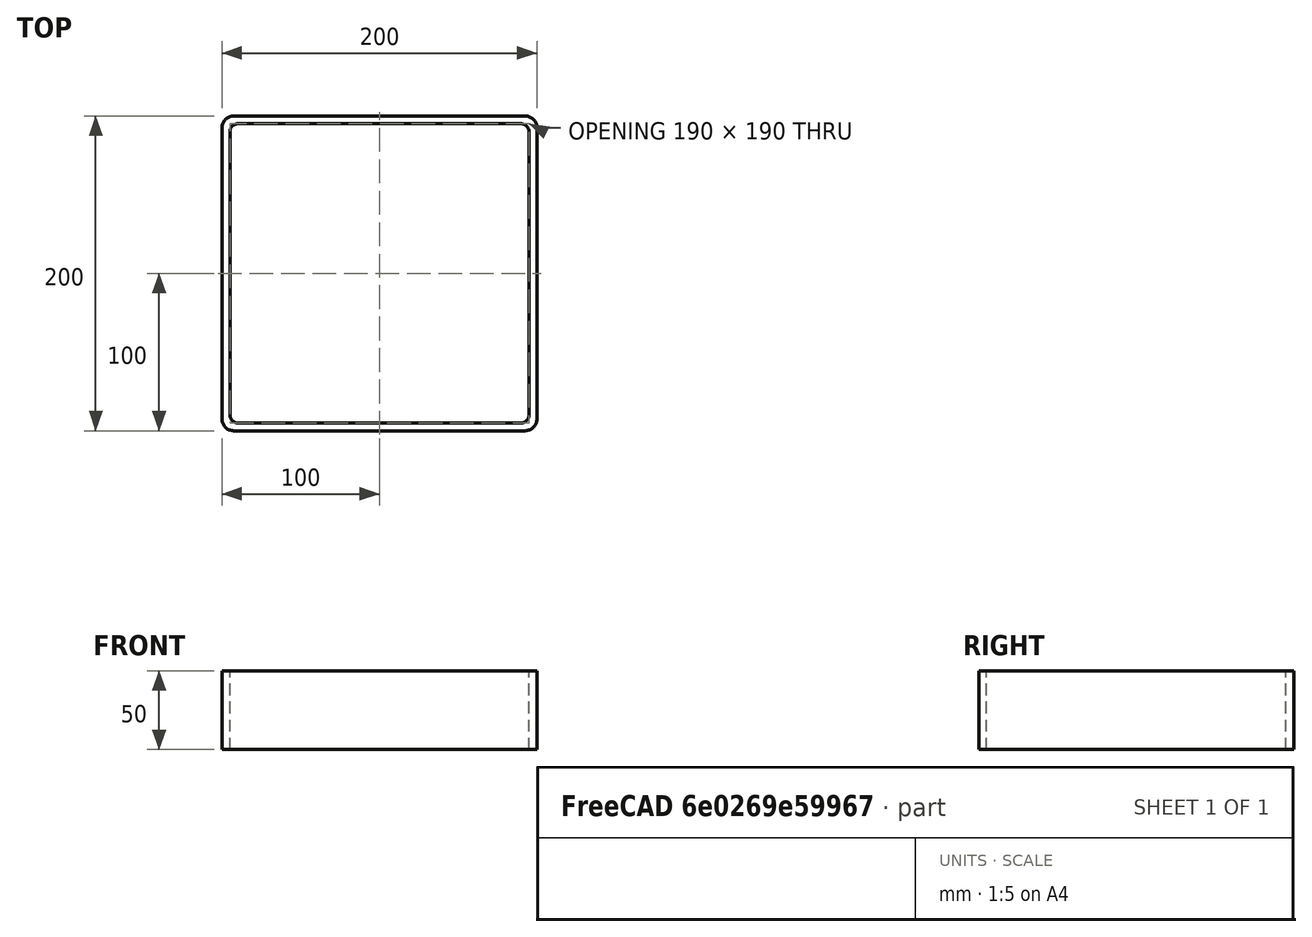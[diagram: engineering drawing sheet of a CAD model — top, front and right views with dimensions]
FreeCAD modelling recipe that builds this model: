
FCSTD DOCUMENT  (FreeCAD 0.15R4671 (Git))
Label: Square hollow section 200x200x5 EN10219 S235JRH
License: All rights reserved
LicenseURL: http://en.wikipedia.org/wiki/All_rights_reserved
objects: Sketcher::SketchObject×1, Part::Extrusion×1
note: 2 computed .brp shape members not serialized (recipe doc carries the construction recipe); baked Part::Feature solids carry a one-line shape summary decoded from their .brp

FEATURE [Sketcher::SketchObject] Sketch
  sketch-geometry (16):
    g0: LineSegment StartX=-90 StartY=95 StartZ=0 EndX=90 EndY=95 EndZ=0
    g1: LineSegment StartX=95 StartY=90 StartZ=0 EndX=95 EndY=-90 EndZ=0
    g2: LineSegment StartX=90 StartY=-95 StartZ=0 EndX=-90 EndY=-95 EndZ=0
    g3: LineSegment StartX=-95 StartY=-90 StartZ=0 EndX=-95 EndY=90 EndZ=0
    g4: LineSegment StartX=-92.5 StartY=100 StartZ=0 EndX=92.5 EndY=100 EndZ=0
    g5: LineSegment StartX=100 StartY=92.5 StartZ=0 EndX=100 EndY=-92.5 EndZ=0
    g6: LineSegment StartX=92.5 StartY=-100 StartZ=0 EndX=-92.5 EndY=-100 EndZ=0
    g7: LineSegment StartX=-100 StartY=-92.5 StartZ=0 EndX=-100 EndY=92.5 EndZ=0
    g8: ArcOfCircle CenterX=-90 CenterY=90 CenterZ=0 NormalX=0 NormalY=0 NormalZ=1 Radius=5 StartAngle=1.5708 EndAngle=3.14159
    g9: ArcOfCircle CenterX=90 CenterY=90 CenterZ=0 NormalX=0 NormalY=0 NormalZ=1 Radius=5 StartAngle=0 EndAngle=1.5708
    g10: ArcOfCircle CenterX=90 CenterY=-90 CenterZ=0 NormalX=0 NormalY=0 NormalZ=1 Radius=5 StartAngle=4.71239 EndAngle=6.28319
    g11: ArcOfCircle CenterX=-90 CenterY=-90 CenterZ=0 NormalX=0 NormalY=0 NormalZ=1 Radius=5 StartAngle=3.14159 EndAngle=4.71239
    g12: ArcOfCircle CenterX=92.5 CenterY=92.5 CenterZ=0 NormalX=0 NormalY=0 NormalZ=1 Radius=7.5 StartAngle=0 EndAngle=1.5708
    g13: ArcOfCircle CenterX=92.5 CenterY=-92.5 CenterZ=0 NormalX=0 NormalY=0 NormalZ=1 Radius=7.5 StartAngle=4.71239 EndAngle=6.28319
    g14: ArcOfCircle CenterX=-92.5 CenterY=-92.5 CenterZ=0 NormalX=0 NormalY=0 NormalZ=1 Radius=7.5 StartAngle=3.14159 EndAngle=4.71239
    g15: ArcOfCircle CenterX=-92.5 CenterY=92.5 CenterZ=0 NormalX=0 NormalY=0 NormalZ=1 Radius=7.5 StartAngle=1.5708 EndAngle=3.14159
  constraints (36):
    c: Horizontal(g2)
    c: Vertical(g3)
    c: Horizontal(g6)
    c: Vertical(g7)
    c: Tangent(g3,g8) = 1.5708
    c: Tangent(g0,g8) = 1.5708
    c: Tangent(g0,g9) = 1.5708
    c: Tangent(g1,g9) = 1.5708
    c: Tangent(g1,g10) = 1.5708
    c: Tangent(g2,g10) = 1.5708
    c: Tangent(g2,g11) = 1.5708
    c: Tangent(g3,g11) = 1.5708
    c: Tangent(g4,g12) = 1.5708
    c: Tangent(g5,g12) = 1.5708
    c: Tangent(g5,g13) = 1.5708
    c: Tangent(g6,g13) = 1.5708
    c: Tangent(g6,g14) = 1.5708
    c: Tangent(g7,g14) = 1.5708
    c: Tangent(g7,g15) = 1.5708
    c: Tangent(g4,g15) = 1.5708
    c: Equal(g9,g8)
    c: Equal(g9,g11)
    c: Equal(g9,g10)
    c: Equal(g12,g15)
    c: Equal(g12,g14)
    c: Equal(g12,g13)
    c: Symmetric(g4,g6,g-1)
    c: Symmetric(g7,g5,g-2)
    c: DistanceY(g4,g6) = -200
    c: DistanceX(g7,g5) = 200
    c: Symmetric(g3,g1,g-2)
    c: Symmetric(g0,g2,g-1)
    c: DistanceY(g0,g4) = 5
    c: DistanceX(g5,g1) = -5
    c: Radius(g9) = 5
    c: Radius(g12) = 7.5
FEATURE [Part::Extrusion] Extrude  label="Square hollow section 200x200x5 EN10219 S235JRH"
  Base = -> Sketch
  Dir = (0,0,50)
  Solid = true
